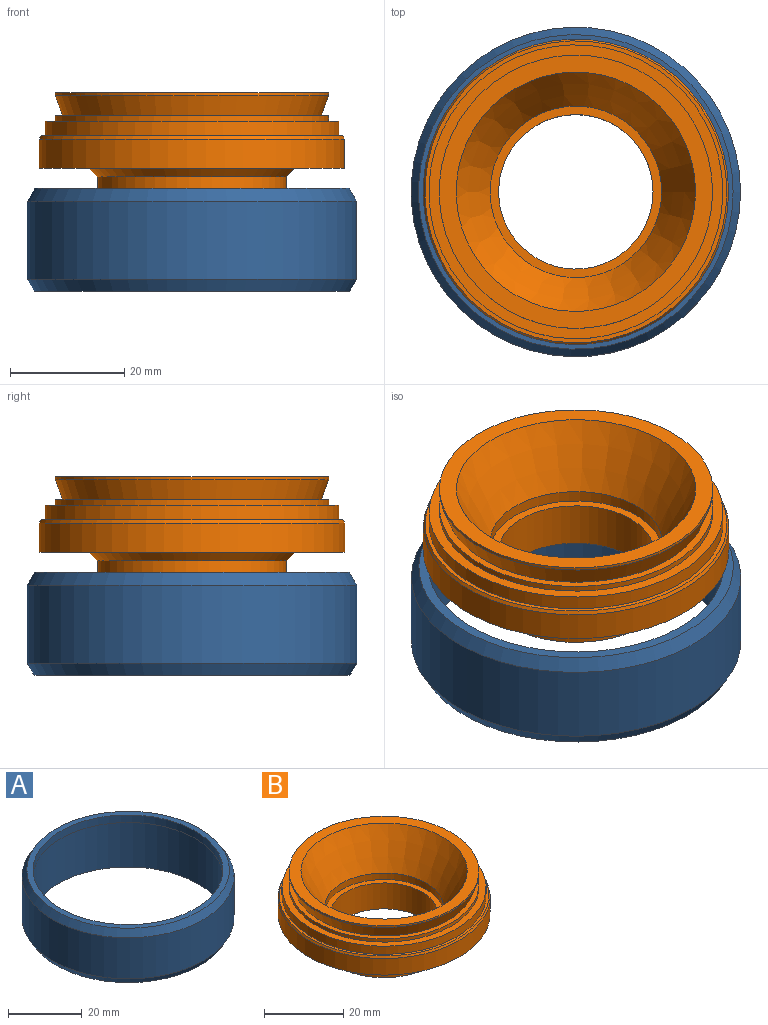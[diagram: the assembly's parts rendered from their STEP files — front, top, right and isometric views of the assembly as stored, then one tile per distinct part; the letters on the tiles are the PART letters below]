
ASSEMBLY  parts=2 mates=1
PART A: 8 faces, bbox 57.6x57.6x18 mm
  f0: cylinder r=26.8mm len=53.6mm, axis (0,0,1), area 2610mm2, adj f1,f7
  f1: plane 55.2x55.2mm, normal (0,0,-1), area 136.7mm2, adj f0,f2
  f2: cone r=28.8mm half-angle=30deg, axis (0,0,1), area 425.2mm2, adj f1,f3
  f3: cylinder r=28.8mm len=57.6mm, axis (0,0,1), area 2473.6mm2, adj f2,f4
  f4: cone r=28.8mm half-angle=30deg, axis (0,0,-1), area 459.9mm2, adj f3,f5
  f5: plane 55x55mm, normal (0,0,1), area 284.7mm2, adj f4,f6
  f6: cylinder r=25.8mm len=51.6mm, axis (0,0,1), area 405.3mm2, adj f5,f7
  f7: plane 53.6x53.6mm, normal (0,0,-1), area 165.2mm2, adj f0,f6
PART B: 18 faces, bbox 53.4x53.4x21.2 mm
  f0: plane 30x30mm, normal (0,0,1), area 134.3mm2, adj f1,f17
  f1: cylinder r=13.5mm len=27mm, axis (0,0,1), area 678.6mm2, adj f0,f2
  f2: plane 33x33mm, normal (0,0,-1), area 282.7mm2, adj f1,f3
  f3: cylinder r=16.5mm len=33mm, axis (0,0,1), area 673.9mm2, adj f2,f4
  f4: cone r=16.5mm half-angle=45deg, axis (0,0,1), area 229.9mm2, adj f3,f5
  f5: plane 53.4x53.4mm, normal (0,0,-1), area 1221.7mm2, adj f4,f6
  f6: cylinder r=26.7mm len=53.4mm, axis (0,0,1), area 855.6mm2, adj f5,f7
  f7: cone r=26.4mm half-angle=26.6deg, axis (0,0,-1), area 111.9mm2, adj f6,f8
  f8: plane 52.8x52.8mm, normal (0,0,1), area 114.6mm2, adj f7,f9
  f9: cylinder r=25.7mm len=51.4mm, axis (0,0,1), area 403.7mm2, adj f8,f10
  f10: plane 51.4x51.4mm, normal (0,0,1), area 280.5mm2, adj f9,f11
  f11: cylinder r=23.9mm len=47.8mm, axis (0,0,1), area 150.2mm2, adj f10,f12
  f12: plane 47.8x47.8mm, normal (0,0,1), area 186.2mm2, adj f11,f13
  f13: cone r=23.9mm half-angle=20deg, axis (0,0,1), area 544.4mm2, adj f12,f14
  f14: cylinder r=23.9mm len=47.8mm, axis (0,0,1), area 75.1mm2, adj f13,f15
  f15: plane 47.8x47.8mm, normal (0,0,1), area 418.4mm2, adj f14,f16
  f16: cone r=20.93mm half-angle=27.9deg, axis (0,0,1), area 1430.4mm2, adj f15,f17
  f17: cylinder r=15mm len=30mm, axis (0,0,1), area 188.5mm2, adj f0,f16
PLACE A t=(6.18,-16.46,6.67)mm
PLACE B t=(6.18,-16.46,46.17)mm
MATE cylindrical B.f1 <-> A.f0  axis (0,0,1) through (6.18,-16.46,17.12)mm
